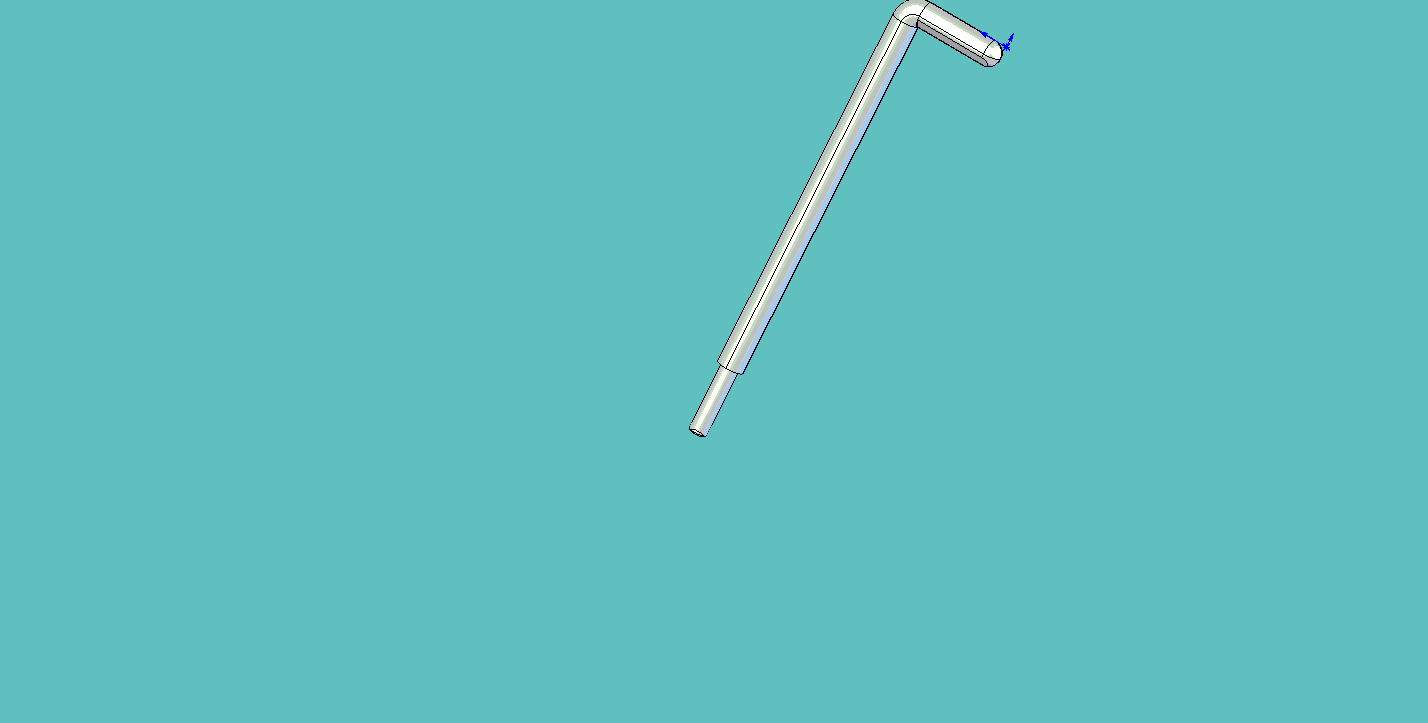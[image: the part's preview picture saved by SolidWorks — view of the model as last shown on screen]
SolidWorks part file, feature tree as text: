
SOLIDWORKS PART (.sldprt)
format: sldprt  version: not decoded by parser v0  size: 186,880 bytes
history: native  units: mm
features: plane x3, sketch x3, extrude x2, fillet x2, material x1, thread x1, cut_extrude x1, chamfer x1 (+8 scaffold rows collapsed)
feature tree (22):
  scaffold x8  (default folders/planes/origin — collapsed)
  material  "Matériau <non spécifié>"
  plane  "Plan de face"
  plane  "Plan de dessus"
  plane  "Plan de droite"
  sketch  "Esquisse2"  dims[D4=6.0mm D5=0.01mm D1=6.0mm D2=25.0mm D3=84.0mm]
  extrude  "Extrusion1"  Depth=6mm
  fillet  "Congé2"  Radius=3mm
  fillet  "Congé9"  Radius=3mm
  sketch  "Esquisse3"  dims[D1=4.0mm]
  extrude  "Extrusion2"  [1 undecoded]
  thread  "Représentation de filetage1"  Diameter=3.3mm  [1 undecoded]
  sketch  "Esquisse4"  dims[c1.D1=~3.571163mm c2.D1=50.0deg c2.D2=~1.454239mm c3.D2=50.0deg c3.D3=1.0mm c3.D4=3.0mm]
  cut_extrude  "Enlèv. mat.-Extru.2"  Depth=18.99mm
  chamfer  "Chanfrein1"  Distance=0.35mm Angle=45deg
decode coverage: 9 of 10 modeling features carry decoded parameters
note: ~ marks probable driven/reference dimensions
note: 2 parameter values undecoded
note: suppression state not decoded; provenance and decode notes live in map.json
